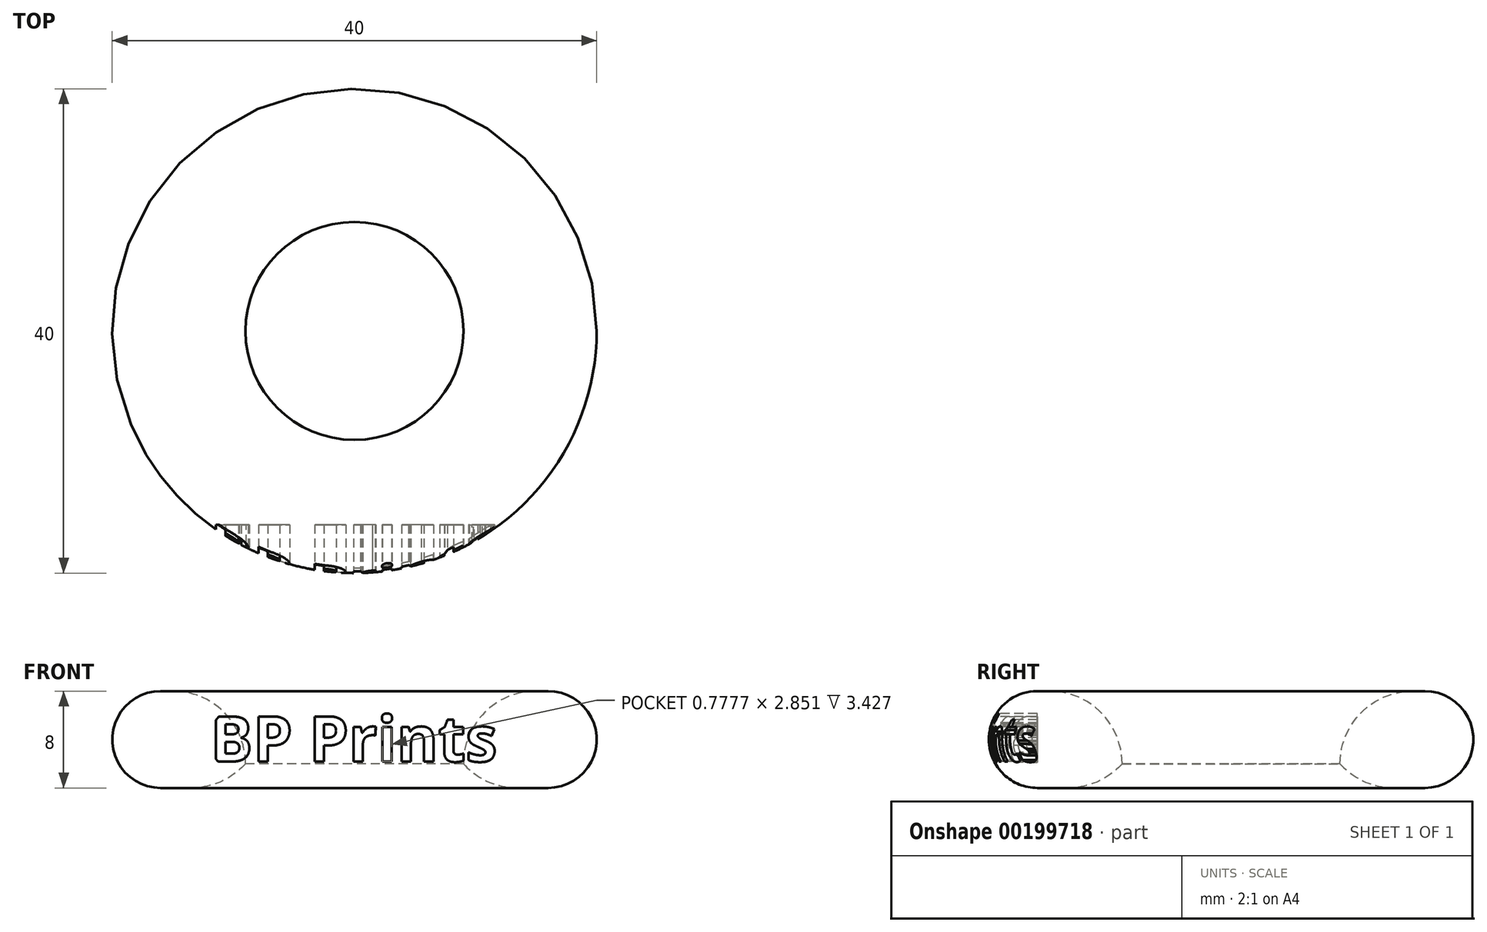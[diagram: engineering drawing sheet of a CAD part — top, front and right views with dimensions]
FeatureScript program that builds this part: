
annotation { "Feature Type Name" : "Feature", "Feature Type Description" : "" }
export const myFeature = defineFeature(function(context is Context, id is Id, definition is map)
    precondition{}
    {
        {
            var Q0;
            Q0=qCreatedBy(makeId("Top.planeOp"),FACE);
            var sketch = newSketch(context, id + "F0", { "sketchPlane" : qUnion([Q0])});
            skCircle(sketch, "E0", {"center": v(0, 0) * mm, "radius": 9 * mm});
            skCircle(sketch, "E1", {"center": v(0, 0) * mm, "radius": 20 * mm});
            skSolve(sketch);
        }
        {
            var Q0;
            Q0=makeQuery(id+"F0.imprint","IMPRINT",FACE,{"disambiguationData":[TD([[makeQuery(id+"F0.imprint","IMPRINT",EDGE,{"derivedFrom":sQuery(id+"F0.wireOp",EDGE,"E0")}),-1.0]])]});
            extrude(context, id + "F1", {"entities" : qUnion([Q0]), "depth" : 8 * mm});
        }
        {
            var Q0;
            Q0=makeQuery(id+"F1.opExtrude","CAP_EDGE",EDGE,{"disambiguationData":[OSD([sQuery(id+"F0.wireOp",EDGE,"E0")])],"isStart":false});
            fillet(context, id + "F2", {"entities" : qUnion([Q0]), "radius" : 6 * mm, "tangentPropagation" : true, "allowEdgeOverflow" : false});
        }
        {
            var Q0;
            Q0=makeQuery(id+"F1.opExtrude","CAP_EDGE",EDGE,{"disambiguationData":[OSD([sQuery(id+"F0.wireOp",EDGE,"E0")])],"isStart":true});
            fillet(context, id + "F3", {"entities" : qUnion([Q0]), "radius" : 6 * mm, "tangentPropagation" : true, "allowEdgeOverflow" : false});
        }
        {
            var Q0;
            Q0=makeQuery(id+"F1.opExtrude","CAP_EDGE",EDGE,{"disambiguationData":[OSD([sQuery(id+"F0.wireOp",EDGE,"E1")])],"isStart":false});
            var Q1;
            Q1=makeQuery(id+"F1.opExtrude","CAP_EDGE",EDGE,{"disambiguationData":[OSD([sQuery(id+"F0.wireOp",EDGE,"E1")])],"isStart":true});
            fillet(context, id + "F4", {"entities" : qUnion([Q0, Q1]), "radius" : 4 * mm, "tangentPropagation" : true, "allowEdgeOverflow" : false});
        }
        {
            var Q0;
            Q0=qCreatedBy(makeId("Front.planeOp"),FACE);
            cPlane(context, id + "F5", {"entities" : qUnion([Q0]), "cplaneType" : CPlaneType.OFFSET, "offset" : 20 * mm, "width" : 150 * mm, "height" : 150 * mm});
        }
        {
            var Q0;
            Q0=qCreatedBy(id+"F5.planeOp",FACE);
            var sketch = newSketch(context, id + "F6", { "sketchPlane" : qUnion([Q0])});
            skText(sketch, "E2", { "text": "BP Prints", "fontName": "OpenSans-Bold.ttf"});
            const initialGuessF6  = {"E2": [-0.01191, 0.00218, 1, 0, 0.00376]};
            skSetInitialGuess(sketch, initialGuessF6);
            skSolve(sketch);
        }
        {
            var Q0;
            Q0 = qSketchRegion(id + "F6", true);
            extrude(context, id + "F7", {"entities" : qUnion([Q0]), "operationType" : NewBodyOperationType.REMOVE, "oppositeDirection" : true, "depth" : 4 * mm});
        }
    });
